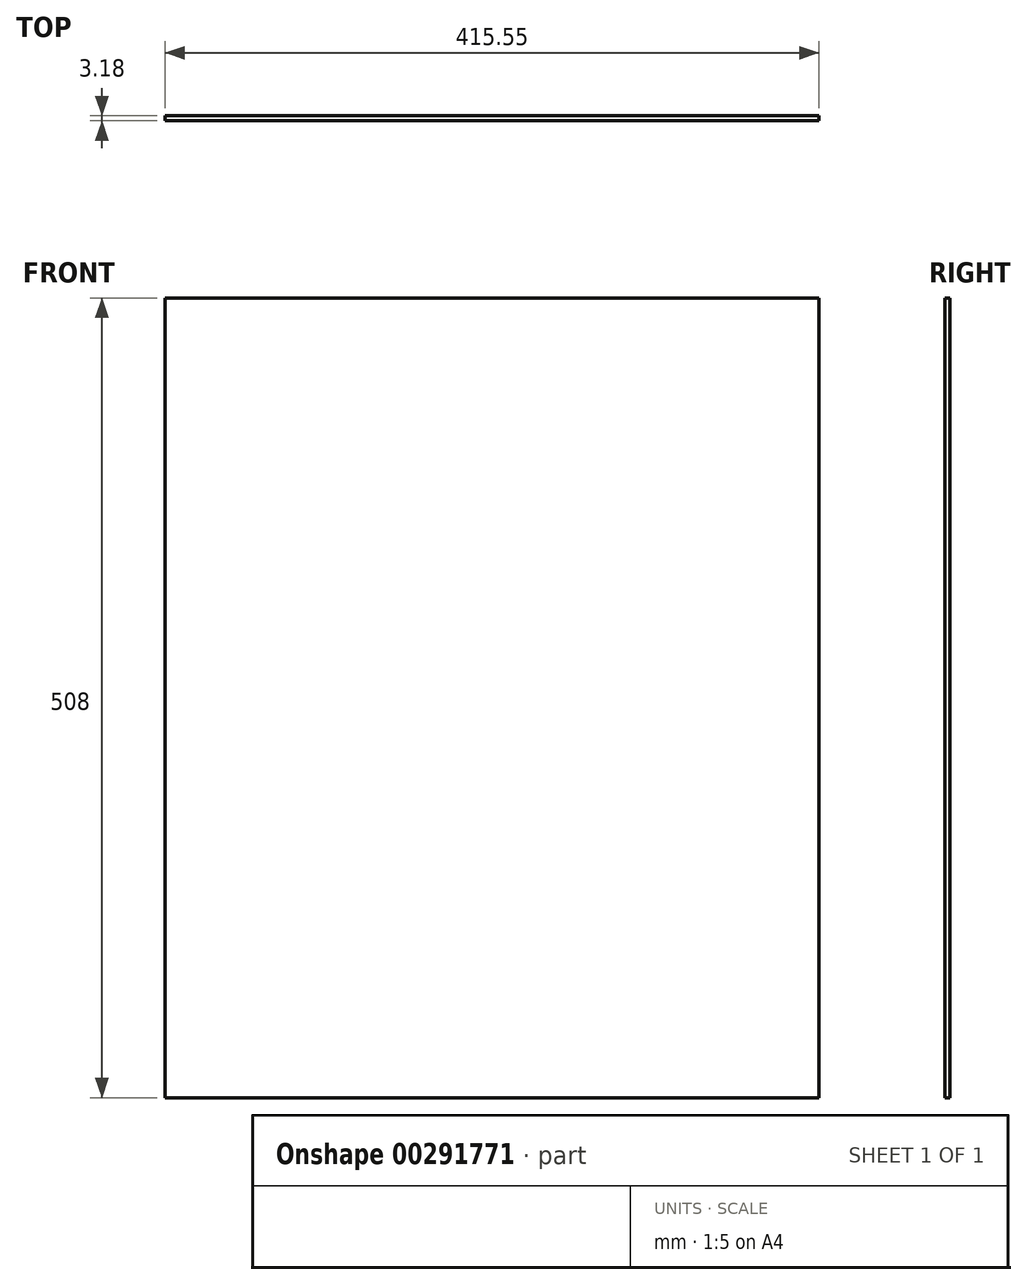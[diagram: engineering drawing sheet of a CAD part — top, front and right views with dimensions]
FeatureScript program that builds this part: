
annotation { "Feature Type Name" : "Feature", "Feature Type Description" : "" }
export const myFeature = defineFeature(function(context is Context, id is Id, definition is map)
    precondition{}
    {
        {
            var Q0;
            Q0=qCreatedBy(makeId("Front.planeOp"),FACE);
            var sketch = newSketch(context, id + "F0", { "sketchPlane" : qUnion([Q0])});
            skLineSegment(sketch, "E0.bottom", {"start": v(-226.9, 251.4) * mm, "end": v(188.64, 251.4) * mm});
            skLineSegment(sketch, "E0.top", {"start": v(-226.9, -256.6) * mm, "end": v(188.64, -256.6) * mm});
            skLineSegment(sketch, "E0.left", {"start": v(-226.9, 251.4) * mm, "end": v(-226.9, -256.6) * mm});
            skLineSegment(sketch, "E0.right", {"start": v(188.64, 251.4) * mm, "end": v(188.64, -256.6) * mm});
            skSolve(sketch);
        }
        {
            var Q0;
            Q0=makeQuery(id+"F0.imprint","IMPRINT",FACE,{"disambiguationData":[TD([[makeQuery(id+"F0.imprint","IMPRINT",EDGE,{"derivedFrom":sQuery(id+"F0.wireOp",EDGE,"E0.bottom")}),-1.0]])]});
            extrude(context, id + "F1", {"entities" : qUnion([Q0]), "endBound" : BoundingType.SYMMETRIC, "depth" : 3.17 * mm});
        }
    });
